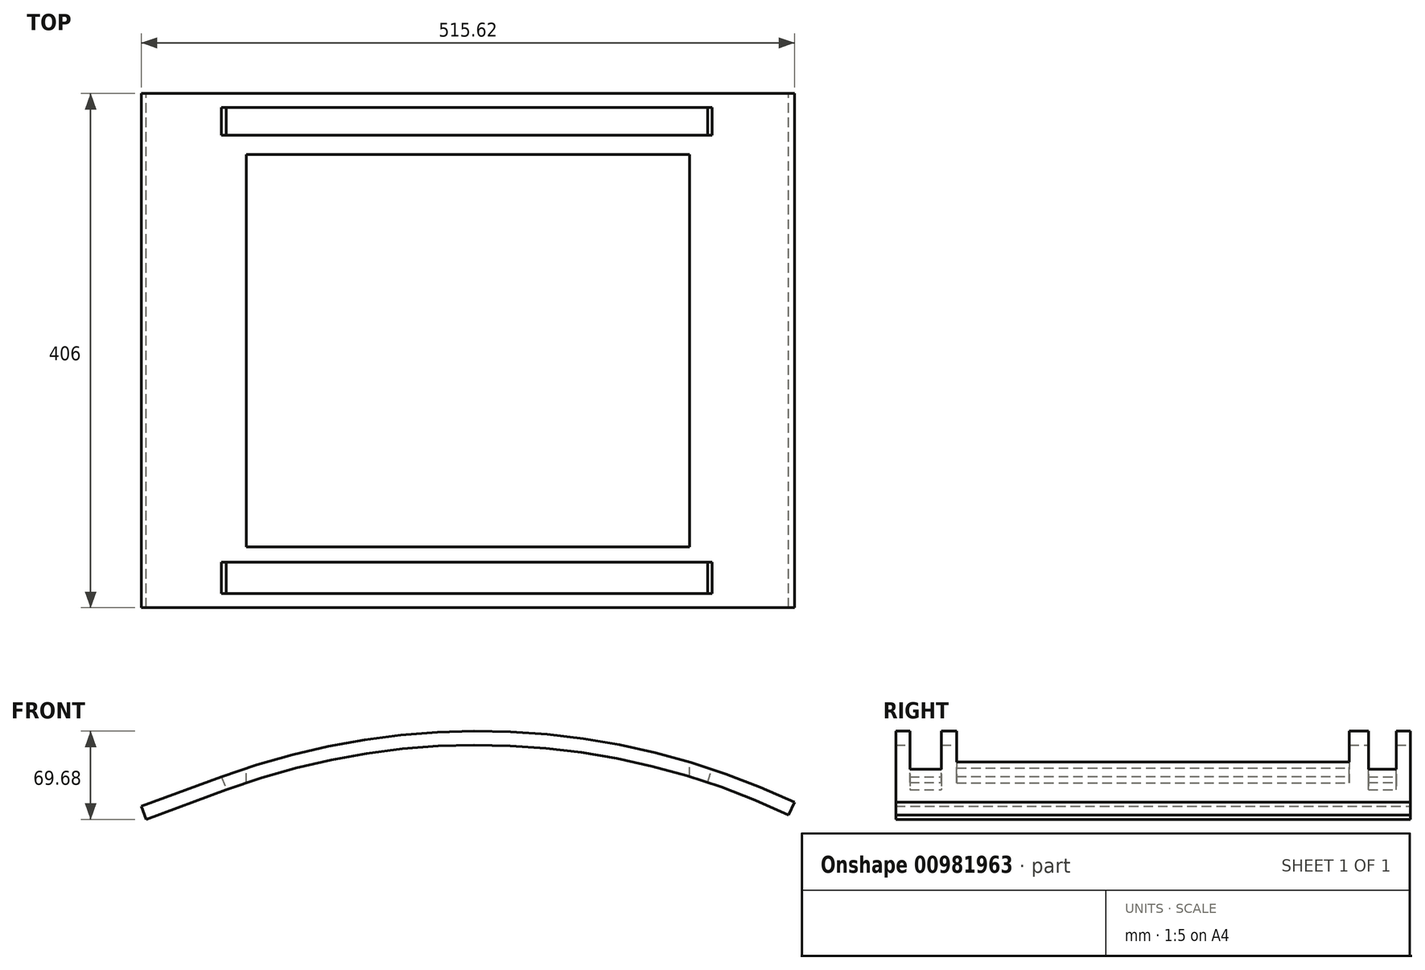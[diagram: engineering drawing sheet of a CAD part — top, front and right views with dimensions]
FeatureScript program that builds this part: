
annotation { "Feature Type Name" : "Feature", "Feature Type Description" : "" }
export const myFeature = defineFeature(function(context is Context, id is Id, definition is map)
    precondition{}
    {
        {
            var Q0;
            Q0=qCreatedBy(makeId("Front.planeOp"),FACE);
            var sketch = newSketch(context, id + "F0", { "sketchPlane" : qUnion([Q0])});
            skArc(sketch, "E0", {"start": v(253.1, -31.32) * mm, "mid": v(33.23, 23.27) * mm, "end": v(-190.64, -11.5) * mm});
            skArc(sketch, "E1", {"start": v(257.81, -21.38) * mm, "mid": v(33.72, 34.26) * mm, "end": v(-194.44, -1.18) * mm});
            skLineSegment(sketch, "E2", {"start": v(-254, -34.84) * mm, "end": v(-190.64, -11.5) * mm});
            skLineSegment(sketch, "E3", {"start": v(-257.81, -24.52) * mm, "end": v(-194.44, -1.18) * mm});
            skLineSegment(sketch, "E4", {"start": v(-257.81, -24.52) * mm, "end": v(-254, -34.84) * mm});
            skLineSegment(sketch, "E5", {"start": v(257.81, -21.38) * mm, "end": v(253.1, -31.32) * mm});
            skSolve(sketch);
        }
        {
            var Q0;
            Q0=makeQuery(id+"F0.imprint","IMPRINT",FACE,{"disambiguationData":[TD([[makeQuery(id+"F0.imprint","IMPRINT",EDGE,{"derivedFrom":sQuery(id+"F0.wireOp",EDGE,"E0")}),-1.0]])]});
            extrude(context, id + "F1", {"entities" : qUnion([Q0]), "depth" : 406 * mm, "offsetDistance" : 25 * mm});
        }
        {
            var Q0;
            Q0=makeQuery(id+"F1.opExtrude","CAP_FACE",FACE,{"disambiguationData":[OSD([sQuery(id+"F0.wireOp",EDGE,"E0"),sQuery(id+"F0.wireOp",EDGE,"E1"),sQuery(id+"F0.wireOp",EDGE,"E2"),sQuery(id+"F0.wireOp",EDGE,"E3"),sQuery(id+"F0.wireOp",EDGE,"E4"),sQuery(id+"F0.wireOp",EDGE,"E5")])],"isStart":false});
            cPlane(context, id + "F2", {"entities" : qUnion([Q0]), "cplaneType" : CPlaneType.OFFSET, "offset" : 11 * mm, "oppositeDirection" : true, "width" : 150 * mm, "height" : 150 * mm});
        }
        {
            var Q0;
            Q0=qCreatedBy(id+"F2.planeOp",FACE);
            var sketch = newSketch(context, id + "F3", { "sketchPlane" : qUnion([Q0])});
            skLineSegment(sketch, "E6", {"start": v(-196.17, 3.51) * mm, "end": v(-188.91, -16.2) * mm});
            skLineSegment(sketch, "E7", {"start": v(187.68, -10.41) * mm, "end": v(194.32, 9.5) * mm});
            skArc(sketch, "E8.0", {"start": v(194.32, 9.5) * mm, "mid": v(-1.43, 39.77) * mm, "end": v(-196.17, 3.51) * mm});
            skArc(sketch, "E9.0", {"start": v(187.68, -10.41) * mm, "mid": v(-1.11, 18.77) * mm, "end": v(-188.91, -16.2) * mm});
            skPoint(sketch, "E10.orphan", {"position": v(-194.44, -1.18) * mm});
            skPoint(sketch, "E11.orphan", {"position": v(-190.64, -11.5) * mm});
            skSolve(sketch);
        }
        {
            var Q0;
            Q0=makeQuery(id+"F3.imprint","IMPRINT",FACE,{"disambiguationData":[TD([[makeQuery(id+"F3.imprint","IMPRINT",EDGE,{"derivedFrom":sQuery(id+"F3.wireOp",EDGE,"E6")}),1.0]])]});
            extrude(context, id + "F4", {"entities" : qUnion([Q0]), "operationType" : NewBodyOperationType.REMOVE, "oppositeDirection" : true, "depth" : 25 * mm, "offsetDistance" : 25 * mm});
        }
        {
            var Q0;
            Q0=makeQuery(id+"F1.opExtrude","CAP_FACE",FACE,{"disambiguationData":[OSD([sQuery(id+"F0.wireOp",EDGE,"E0"),sQuery(id+"F0.wireOp",EDGE,"E1"),sQuery(id+"F0.wireOp",EDGE,"E2"),sQuery(id+"F0.wireOp",EDGE,"E3"),sQuery(id+"F0.wireOp",EDGE,"E4"),sQuery(id+"F0.wireOp",EDGE,"E5")])],"isStart":true});
            cPlane(context, id + "F5", {"entities" : qUnion([Q0]), "cplaneType" : CPlaneType.OFFSET, "offset" : 11 * mm, "oppositeDirection" : true, "width" : 150 * mm, "height" : 150 * mm});
        }
        {
            var Q0;
            Q0=qCreatedBy(id+"F5.planeOp",FACE);
            var sketch = newSketch(context, id + "F6", { "sketchPlane" : qUnion([Q0])});
            skLineSegment(sketch, "E12.0", {"start": v(196.17, 3.51) * mm, "end": v(188.91, -16.2) * mm});
            skLineSegment(sketch, "E12.1", {"start": v(-187.68, -10.41) * mm, "end": v(-194.32, 9.5) * mm});
            skArc(sketch, "E12.2", {"start": v(-194.32, 9.5) * mm, "mid": v(1.43, 39.77) * mm, "end": v(196.17, 3.51) * mm});
            skArc(sketch, "E12.3", {"start": v(-187.68, -10.41) * mm, "mid": v(1.11, 18.77) * mm, "end": v(188.91, -16.2) * mm});
            skPoint(sketch, "E12.4", {"position": v(194.44, -1.18) * mm});
            skPoint(sketch, "E12.5", {"position": v(190.64, -11.5) * mm});
            skSolve(sketch);
        }
        {
            var Q0;
            Q0 = qSketchRegion(id + "F6", true);
            extrude(context, id + "F7", {"entities" : qUnion([Q0]), "operationType" : NewBodyOperationType.REMOVE, "oppositeDirection" : true, "depth" : 22 * mm, "offsetDistance" : 25 * mm});
        }
        {
            var Q0;
            Q0=qCreatedBy(makeId("Top.planeOp"),FACE);
            cPlane(context, id + "F8", {"entities" : qUnion([Q0]), "cplaneType" : CPlaneType.OFFSET, "offset" : 100 * mm, "width" : 150 * mm, "height" : 150 * mm});
        }
        {
            var Q0;
            Q0=qCreatedBy(id+"F8.planeOp",FACE);
            var sketch = newSketch(context, id + "F9", { "sketchPlane" : qUnion([Q0])});
            skLineSegment(sketch, "E13.bottom", {"start": v(-175, -48) * mm, "end": v(175, -48) * mm});
            skLineSegment(sketch, "E13.top", {"start": v(-175, -358) * mm, "end": v(175, -358) * mm});
            skLineSegment(sketch, "E13.left", {"start": v(-175, -48) * mm, "end": v(-175, -358) * mm});
            skLineSegment(sketch, "E13.right", {"start": v(175, -48) * mm, "end": v(175, -358) * mm});
            skLineSegment(sketch, "E14.0", {"start": v(-257.81, -406) * mm, "end": v(-257.81, 0) * mm, "construction": true});
            skLineSegment(sketch, "E15.0", {"start": v(257.81, -406) * mm, "end": v(257.81, 0) * mm, "construction": true});
            skLineSegment(sketch, "E16", {"start": v(-257.81, -406) * mm, "end": v(257.81, -406) * mm, "construction": true});
            skLineSegment(sketch, "E17", {"start": v(0, -406) * mm, "end": v(0, -322.07) * mm, "construction": true});
            skLineSegment(sketch, "E18", {"start": v(-257.81, -203) * mm, "end": v(-117.57, -203) * mm, "construction": true});
            skSolve(sketch);
        }
        {
            var Q0;
            Q0=makeQuery(id+"F9.imprint","IMPRINT",FACE,{"disambiguationData":[TD([[makeQuery(id+"F9.imprint","IMPRINT",EDGE,{"derivedFrom":sQuery(id+"F9.wireOp",EDGE,"E13.bottom")}),-1.0]])]});
            extrude(context, id + "F10", {"entities" : qUnion([Q0]), "operationType" : NewBodyOperationType.REMOVE, "oppositeDirection" : true, "depth" : 150 * mm, "offsetDistance" : 25 * mm});
        }
    });
